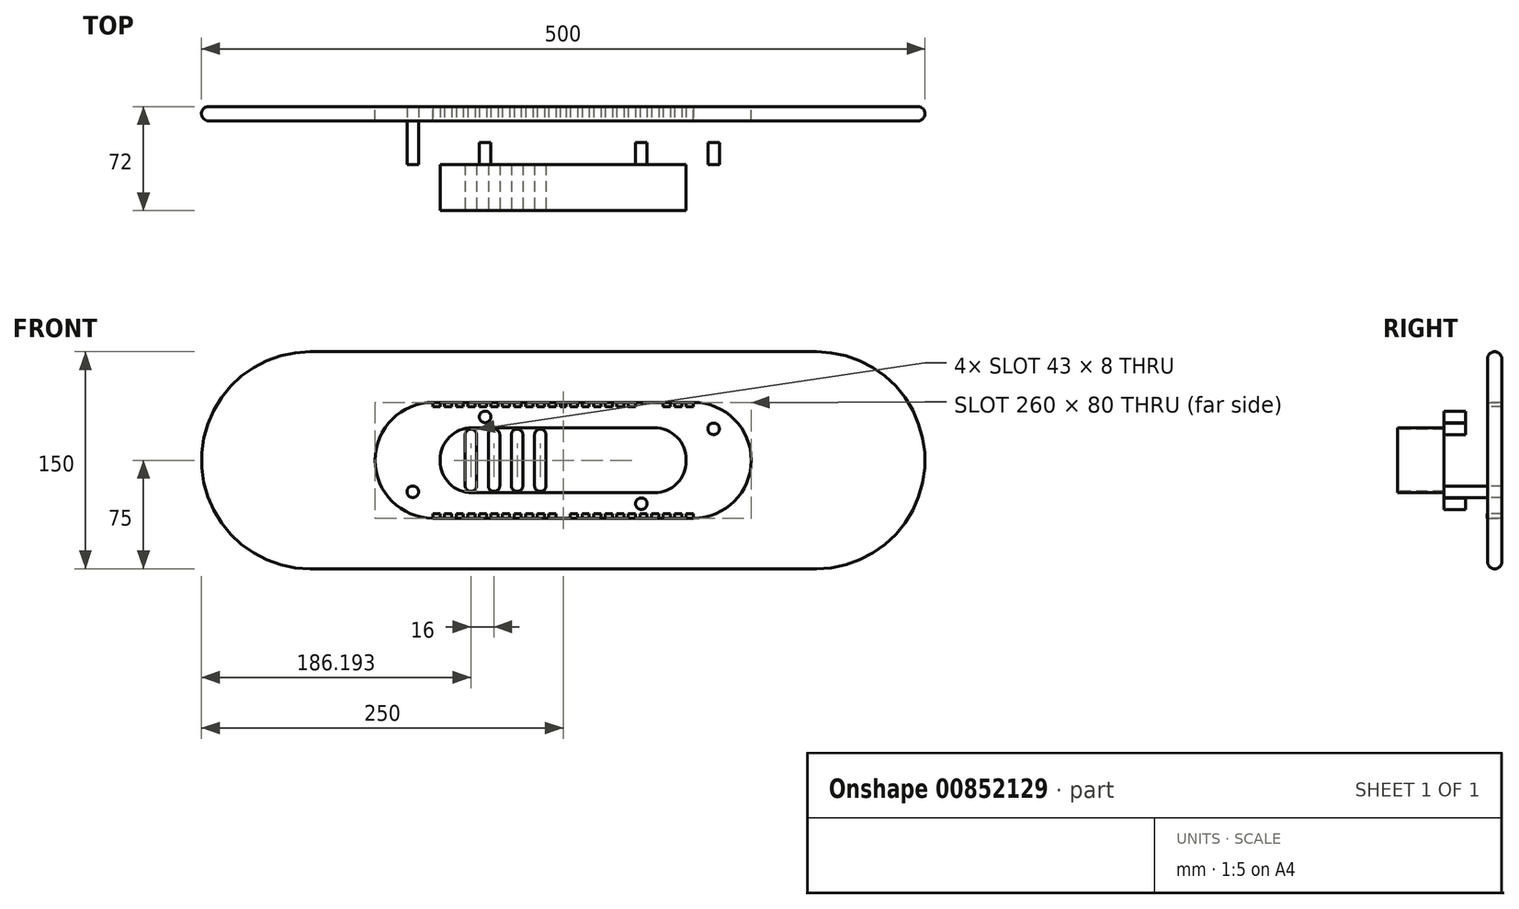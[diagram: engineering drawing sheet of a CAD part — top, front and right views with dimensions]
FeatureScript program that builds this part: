
annotation { "Feature Type Name" : "Feature", "Feature Type Description" : "" }
export const myFeature = defineFeature(function(context is Context, id is Id, definition is map)
    precondition{}
    {
        {
            var Q0;
            Q0=qCreatedBy(makeId("Front.planeOp"),FACE);
            var sketch = newSketch(context, id + "F0", { "sketchPlane" : qUnion([Q0])});
            skLineSegment(sketch, "E0.bottom", {"start": v(175, -75) * mm, "end": v(-175, -75) * mm});
            skLineSegment(sketch, "E0.top", {"start": v(175, 75) * mm, "end": v(-175, 75) * mm});
            skLineSegment(sketch, "E0.left", {"start": v(250, 0) * mm, "end": v(250, 0) * mm});
            skLineSegment(sketch, "E0.right", {"start": v(-250, 0) * mm, "end": v(-250, 0) * mm});
            skPoint(sketch, "E0.middle", {"position": v(0, 0) * mm});
            skPoint(sketch, "E1.visualSharp", {"position": v(-250, 75) * mm});
            skArc(sketch, "E1.filletArc", {"start": v(-175, 75) * mm, "mid": v(-228.03, 53.03) * mm, "end": v(-250, 0) * mm});
            skPoint(sketch, "E2.visualSharp", {"position": v(-250, -75) * mm});
            skArc(sketch, "E2.filletArc", {"start": v(-250, 0) * mm, "mid": v(-228.03, -53.03) * mm, "end": v(-175, -75) * mm});
            skPoint(sketch, "E3.visualSharp", {"position": v(250, -75) * mm});
            skArc(sketch, "E3.filletArc", {"start": v(175, -75) * mm, "mid": v(228.03, -53.03) * mm, "end": v(250, 0) * mm});
            skPoint(sketch, "E4.visualSharp", {"position": v(250, 75) * mm});
            skArc(sketch, "E4.filletArc", {"start": v(250, 0) * mm, "mid": v(228.03, 53.03) * mm, "end": v(175, 75) * mm});
            skLineSegment(sketch, "E5.bottom", {"start": v(90, -40) * mm, "end": v(-90, -40) * mm});
            skLineSegment(sketch, "E5.top", {"start": v(90, 40) * mm, "end": v(-90, 40) * mm});
            skLineSegment(sketch, "E5.left", {"start": v(130, 0) * mm, "end": v(130, 0) * mm});
            skLineSegment(sketch, "E5.right", {"start": v(-130, 0) * mm, "end": v(-130, 0) * mm});
            skPoint(sketch, "E6.visualSharp", {"position": v(-130, 40) * mm});
            skArc(sketch, "E6.filletArc", {"start": v(-90, 40) * mm, "mid": v(-118.28, 28.28) * mm, "end": v(-130, 0) * mm});
            skPoint(sketch, "E7.visualSharp", {"position": v(-130, -40) * mm});
            skArc(sketch, "E7.filletArc", {"start": v(-130, 0) * mm, "mid": v(-118.28, -28.28) * mm, "end": v(-90, -40) * mm});
            skPoint(sketch, "E8.visualSharp", {"position": v(130, 40) * mm});
            skArc(sketch, "E8.filletArc", {"start": v(130, 0) * mm, "mid": v(118.28, 28.28) * mm, "end": v(90, 40) * mm});
            skPoint(sketch, "E9.visualSharp", {"position": v(130, -40) * mm});
            skArc(sketch, "E9.filletArc", {"start": v(90, -40) * mm, "mid": v(118.28, -28.28) * mm, "end": v(130, 0) * mm});
            skLineSegment(sketch, "E10.bottom", {"start": v(63, -22.5) * mm, "end": v(-63, -22.5) * mm});
            skLineSegment(sketch, "E10.top", {"start": v(63, 22.5) * mm, "end": v(-63, 22.5) * mm});
            skLineSegment(sketch, "E10.left", {"start": v(85, -0.5) * mm, "end": v(85, 0.5) * mm});
            skLineSegment(sketch, "E10.right", {"start": v(-85, -0.5) * mm, "end": v(-85, 0.5) * mm});
            skPoint(sketch, "E11.visualSharp", {"position": v(-85, 22.5) * mm});
            skArc(sketch, "E11.filletArc", {"start": v(-63, 22.5) * mm, "mid": v(-78.56, 16.06) * mm, "end": v(-85, 0.5) * mm});
            skPoint(sketch, "E12.visualSharp", {"position": v(-85, -22.5) * mm});
            skArc(sketch, "E12.filletArc", {"start": v(-85, -0.5) * mm, "mid": v(-78.56, -16.06) * mm, "end": v(-63, -22.5) * mm});
            skPoint(sketch, "E13.visualSharp", {"position": v(85, -22.5) * mm});
            skArc(sketch, "E13.filletArc", {"start": v(63, -22.5) * mm, "mid": v(78.56, -16.06) * mm, "end": v(85, -0.5) * mm});
            skPoint(sketch, "E14.visualSharp", {"position": v(85, 22.5) * mm});
            skArc(sketch, "E14.filletArc", {"start": v(85, 0.5) * mm, "mid": v(78.56, 16.06) * mm, "end": v(63, 22.5) * mm});
            skSolve(sketch);
        }
        {
            var Q0;
            Q0=makeQuery(id+"F0.imprint","IMPRINT",FACE,{"disambiguationData":[TD([[makeQuery(id+"F0.imprint","IMPRINT",EDGE,{"derivedFrom":sQuery(id+"F0.wireOp",EDGE,"E0.bottom")}),-1.0]])]});
            extrude(context, id + "F1", {"entities" : qUnion([Q0]), "depth" : 10 * mm, "offsetDistance" : 25 * mm});
        }
        {
            var Q0;
            Q0=makeQuery(id+"F0.imprint","IMPRINT",FACE,{"disambiguationData":[TD([[makeQuery(id+"F0.imprint","IMPRINT",EDGE,{"derivedFrom":sQuery(id+"F0.wireOp",EDGE,"E5.bottom")}),-1.0]])]});
            extrude(context, id + "F2", {"entities" : qUnion([Q0]), "depth" : 40 * mm, "offsetDistance" : 25 * mm});
        }
        {
            var Q0;
            Q0=makeQuery(id+"F0.imprint","IMPRINT",FACE,{"disambiguationData":[TD([[makeQuery(id+"F0.imprint","IMPRINT",EDGE,{"derivedFrom":sQuery(id+"F0.wireOp",EDGE,"E10.bottom")}),-1.0]])]});
            extrude(context, id + "F3", {"entities" : qUnion([Q0]), "depth" : 72 * mm, "offsetDistance" : 25 * mm});
        }
        {
            var Q0;
            Q0=makeQuery(id+"F1.opExtrude","CAP_EDGE",EDGE,{"disambiguationData":[OSD([sQuery(id+"F0.wireOp",EDGE,"E1.filletArc"),sQuery(id+"F0.wireOp",EDGE,"E2.filletArc")])],"isStart":true});
            var Q1;
            Q1=makeQuery(id+"F1.opExtrude","CAP_EDGE",EDGE,{"disambiguationData":[OSD([sQuery(id+"F0.wireOp",EDGE,"E1.filletArc"),sQuery(id+"F0.wireOp",EDGE,"E2.filletArc")])],"isStart":false});
            fillet(context, id + "F4", {"entities" : qUnion([Q0, Q1]), "radius" : 5 * mm, "tangentPropagation" : true, "allowEdgeOverflow" : false});
        }
        {
            var Q0;
            Q0=makeQuery(id+"F2.opExtrude","SWEPT_FACE",FACE,{"disambiguationData":[OSD([sQuery(id+"F0.wireOp",EDGE,"E5.bottom")])]});
            var sketch = newSketch(context, id + "F5", { "sketchPlane" : qUnion([Q0])});
            skLineSegment(sketch, "E15.bottom", {"start": v(-90, 40) * mm, "end": v(-1.81, 40) * mm});
            skLineSegment(sketch, "E15.top", {"start": v(-90, 10.14) * mm, "end": v(-1.81, 10.14) * mm});
            skLineSegment(sketch, "E15.left", {"start": v(-90, 40) * mm, "end": v(-90, 10.14) * mm});
            skLineSegment(sketch, "E15.right", {"start": v(90, 40) * mm, "end": v(90, 10.14) * mm});
            skLineSegment(sketch, "E16.bottom", {"start": v(-85, 40) * mm, "end": v(-82, 40) * mm});
            skLineSegment(sketch, "E16.top", {"start": v(-85, 10.14) * mm, "end": v(-82, 10.14) * mm});
            skLineSegment(sketch, "E16.left", {"start": v(-85, 40) * mm, "end": v(-85, 10.14) * mm});
            skLineSegment(sketch, "E16.right", {"start": v(-82, 40) * mm, "end": v(-82, 10.14) * mm});
            skLineSegment(sketch, "E17.bottom", {"start": v(-77, 40) * mm, "end": v(-74, 40) * mm});
            skLineSegment(sketch, "E17.top", {"start": v(-77, 10.14) * mm, "end": v(-74, 10.14) * mm});
            skLineSegment(sketch, "E17.left", {"start": v(-77, 40) * mm, "end": v(-77, 10.14) * mm});
            skLineSegment(sketch, "E17.right", {"start": v(-74, 40) * mm, "end": v(-74, 10.14) * mm});
            skLineSegment(sketch, "E18.bottom", {"start": v(-69, 40) * mm, "end": v(-66, 40) * mm});
            skLineSegment(sketch, "E18.top", {"start": v(-69, 10.14) * mm, "end": v(-66, 10.14) * mm});
            skLineSegment(sketch, "E18.left", {"start": v(-69, 40) * mm, "end": v(-69, 10.14) * mm});
            skLineSegment(sketch, "E18.right", {"start": v(-66, 40) * mm, "end": v(-66, 10.14) * mm});
            skLineSegment(sketch, "E19.bottom", {"start": v(-61, 40) * mm, "end": v(-58, 40) * mm});
            skLineSegment(sketch, "E19.top", {"start": v(-61, 10.14) * mm, "end": v(-58, 10.14) * mm});
            skLineSegment(sketch, "E19.left", {"start": v(-61, 40) * mm, "end": v(-61, 10.14) * mm});
            skLineSegment(sketch, "E19.right", {"start": v(-58, 40) * mm, "end": v(-58, 10.14) * mm});
            skLineSegment(sketch, "E20.bottom", {"start": v(-53, 40) * mm, "end": v(-50, 40) * mm});
            skLineSegment(sketch, "E20.top", {"start": v(-53, 10.14) * mm, "end": v(-50, 10.14) * mm});
            skLineSegment(sketch, "E20.left", {"start": v(-53, 40) * mm, "end": v(-53, 10.14) * mm});
            skLineSegment(sketch, "E20.right", {"start": v(-50, 40) * mm, "end": v(-50, 10.14) * mm});
            skLineSegment(sketch, "E21.bottom", {"start": v(-45, 40) * mm, "end": v(-42, 40) * mm});
            skLineSegment(sketch, "E21.top", {"start": v(-45, 10.14) * mm, "end": v(-42, 10.14) * mm});
            skLineSegment(sketch, "E21.left", {"start": v(-42, 40) * mm, "end": v(-42, 10.14) * mm});
            skLineSegment(sketch, "E21.right", {"start": v(-45, 40) * mm, "end": v(-45, 10.14) * mm});
            skLineSegment(sketch, "E22.bottom", {"start": v(-37, 40) * mm, "end": v(-34, 40) * mm});
            skLineSegment(sketch, "E22.top", {"start": v(-37, 10.14) * mm, "end": v(-34, 10.14) * mm});
            skLineSegment(sketch, "E22.left", {"start": v(-37, 40) * mm, "end": v(-37, 10.14) * mm});
            skLineSegment(sketch, "E22.right", {"start": v(-34, 40) * mm, "end": v(-34, 10.14) * mm});
            skLineSegment(sketch, "E23.bottom", {"start": v(-29, 40) * mm, "end": v(-26, 40) * mm});
            skLineSegment(sketch, "E23.top", {"start": v(-29, 10.14) * mm, "end": v(-26, 10.14) * mm});
            skLineSegment(sketch, "E23.left", {"start": v(-29, 40) * mm, "end": v(-29, 10.14) * mm});
            skLineSegment(sketch, "E23.right", {"start": v(-26, 40) * mm, "end": v(-26, 10.14) * mm});
            skLineSegment(sketch, "E24.bottom", {"start": v(-21, 40) * mm, "end": v(-18, 40) * mm});
            skLineSegment(sketch, "E24.top", {"start": v(-21, 10.14) * mm, "end": v(-18, 10.14) * mm});
            skLineSegment(sketch, "E24.left", {"start": v(-21, 40) * mm, "end": v(-21, 10.14) * mm});
            skLineSegment(sketch, "E24.right", {"start": v(-18, 40) * mm, "end": v(-18, 10.14) * mm});
            skLineSegment(sketch, "E25.bottom", {"start": v(-13, 40) * mm, "end": v(-10, 40) * mm});
            skLineSegment(sketch, "E25.top", {"start": v(-13, 10.14) * mm, "end": v(-10, 10.14) * mm});
            skLineSegment(sketch, "E25.left", {"start": v(-13, 40) * mm, "end": v(-13, 10.14) * mm});
            skLineSegment(sketch, "E25.right", {"start": v(-10, 40) * mm, "end": v(-10, 10.14) * mm});
            skLineSegment(sketch, "E26.bottom", {"start": v(-5, 40) * mm, "end": v(1.84, 40) * mm});
            skLineSegment(sketch, "E26.top", {"start": v(-5, 10.14) * mm, "end": v(1.84, 10.14) * mm});
            skLineSegment(sketch, "E26.left", {"start": v(-5, 40) * mm, "end": v(-5, 10.14) * mm});
            skLineSegment(sketch, "E27.bottom", {"start": v(-2, 40) * mm, "end": v(-1.81, 40) * mm});
            skLineSegment(sketch, "E27.top", {"start": v(-2, 10.14) * mm, "end": v(-1.81, 10.14) * mm});
            skLineSegment(sketch, "E27.left", {"start": v(-2, 40) * mm, "end": v(-2, 10.14) * mm});
            skLineSegment(sketch, "E28.trimOffspring", {"start": v(1.84, 10.14) * mm, "end": v(90, 10.14) * mm});
            skLineSegment(sketch, "E29.trimOffspring", {"start": v(1.84, 40) * mm, "end": v(90, 40) * mm});
            skLineSegment(sketch, "E30.MirrorCS", {"start": v(2, 10.14) * mm, "end": v(1.81, 10.14) * mm});
            skLineSegment(sketch, "E31.MirrorCS", {"start": v(2, 40) * mm, "end": v(1.81, 40) * mm});
            skLineSegment(sketch, "E32.MirrorCS", {"start": v(45, 40) * mm, "end": v(42, 40) * mm});
            skLineSegment(sketch, "E33.MirrorCS", {"start": v(53, 10.14) * mm, "end": v(50, 10.14) * mm});
            skLineSegment(sketch, "E34.MirrorCS", {"start": v(21, 40) * mm, "end": v(18, 40) * mm});
            skLineSegment(sketch, "E35.MirrorCS", {"start": v(90, 10.14) * mm, "end": v(1.81, 10.14) * mm});
            skLineSegment(sketch, "E36.MirrorCS", {"start": v(53, 40) * mm, "end": v(50, 40) * mm});
            skLineSegment(sketch, "E37.MirrorCS", {"start": v(13, 10.14) * mm, "end": v(10, 10.14) * mm});
            skLineSegment(sketch, "E38.MirrorCS", {"start": v(61, 10.14) * mm, "end": v(58, 10.14) * mm});
            skLineSegment(sketch, "E39.MirrorCS", {"start": v(77, 40) * mm, "end": v(74, 40) * mm});
            skLineSegment(sketch, "E40.MirrorCS", {"start": v(37, 40) * mm, "end": v(34, 40) * mm});
            skLineSegment(sketch, "E41.MirrorCS", {"start": v(69, 10.14) * mm, "end": v(66, 10.14) * mm});
            skLineSegment(sketch, "E42.MirrorCS", {"start": v(21, 10.14) * mm, "end": v(18, 10.14) * mm});
            skLineSegment(sketch, "E43.MirrorCS", {"start": v(29, 40) * mm, "end": v(26, 40) * mm});
            skLineSegment(sketch, "E44.MirrorCS", {"start": v(85, 10.14) * mm, "end": v(82, 10.14) * mm});
            skLineSegment(sketch, "E45.MirrorCS", {"start": v(29, 10.14) * mm, "end": v(26, 10.14) * mm});
            skLineSegment(sketch, "E46.MirrorCS", {"start": v(69, 40) * mm, "end": v(66, 40) * mm});
            skLineSegment(sketch, "E47.MirrorCS", {"start": v(90, 40) * mm, "end": v(1.81, 40) * mm});
            skLineSegment(sketch, "E48.MirrorCS", {"start": v(85, 40) * mm, "end": v(82, 40) * mm});
            skLineSegment(sketch, "E49.MirrorCS", {"start": v(13, 40) * mm, "end": v(10, 40) * mm});
            skLineSegment(sketch, "E50.MirrorCS", {"start": v(45, 10.14) * mm, "end": v(42, 10.14) * mm});
            skLineSegment(sketch, "E51.MirrorCS", {"start": v(61, 40) * mm, "end": v(58, 40) * mm});
            skLineSegment(sketch, "E52.MirrorCS", {"start": v(77, 10.14) * mm, "end": v(74, 10.14) * mm});
            skLineSegment(sketch, "E53.MirrorCS", {"start": v(37, 10.14) * mm, "end": v(34, 10.14) * mm});
            skLineSegment(sketch, "E54.MirrorCS", {"start": v(66, 40) * mm, "end": v(66, 10.14) * mm});
            skLineSegment(sketch, "E55.MirrorCS", {"start": v(61, 40) * mm, "end": v(61, 10.14) * mm});
            skLineSegment(sketch, "E56.MirrorCS", {"start": v(58, 40) * mm, "end": v(58, 10.14) * mm});
            skLineSegment(sketch, "E57.MirrorCS", {"start": v(50, 40) * mm, "end": v(50, 10.14) * mm});
            skLineSegment(sketch, "E58.MirrorCS", {"start": v(13, 40) * mm, "end": v(13, 10.14) * mm});
            skLineSegment(sketch, "E59.MirrorCS", {"start": v(2, 40) * mm, "end": v(2, 10.14) * mm});
            skLineSegment(sketch, "E60.MirrorCS", {"start": v(21, 40) * mm, "end": v(21, 10.14) * mm});
            skLineSegment(sketch, "E61.MirrorCS", {"start": v(45, 40) * mm, "end": v(45, 10.14) * mm});
            skLineSegment(sketch, "E62.MirrorCS", {"start": v(37, 40) * mm, "end": v(37, 10.14) * mm});
            skLineSegment(sketch, "E63.MirrorCS", {"start": v(85, 40) * mm, "end": v(85, 10.14) * mm});
            skLineSegment(sketch, "E64.MirrorCS", {"start": v(42, 40) * mm, "end": v(42, 10.14) * mm});
            skLineSegment(sketch, "E65.MirrorCS", {"start": v(18, 40) * mm, "end": v(18, 10.14) * mm});
            skLineSegment(sketch, "E66.MirrorCS", {"start": v(26, 40) * mm, "end": v(26, 10.14) * mm});
            skLineSegment(sketch, "E67.MirrorCS", {"start": v(29, 40) * mm, "end": v(29, 10.14) * mm});
            skLineSegment(sketch, "E68.MirrorCS", {"start": v(77, 40) * mm, "end": v(77, 10.14) * mm});
            skLineSegment(sketch, "E69.MirrorCS", {"start": v(10, 40) * mm, "end": v(10, 10.14) * mm});
            skLineSegment(sketch, "E70.MirrorCS", {"start": v(34, 40) * mm, "end": v(34, 10.14) * mm});
            skLineSegment(sketch, "E71.MirrorCS", {"start": v(82, 40) * mm, "end": v(82, 10.14) * mm});
            skLineSegment(sketch, "E72.MirrorCS", {"start": v(53, 40) * mm, "end": v(53, 10.14) * mm});
            skLineSegment(sketch, "E73.MirrorCS", {"start": v(74, 40) * mm, "end": v(74, 10.14) * mm});
            skLineSegment(sketch, "E74.MirrorCS", {"start": v(5, 40) * mm, "end": v(5, 10.14) * mm});
            skLineSegment(sketch, "E75.MirrorCS", {"start": v(69, 40) * mm, "end": v(69, 10.14) * mm});
            skSolve(sketch);
        }
        {
            var Q0;
            {var subQ0=sQuery(id+"F5.wireOp",EDGE,"E15.left");Q0=makeQuery(id+"F5.imprint","IMPRINT",FACE,{"disambiguationData":[TD([[makeQuery(id+"F5.imprint","IMPRINT",EDGE,{"derivedFrom":subQ0}),1.0]])]});}
            var Q1;
            {var subQ0=sQuery(id+"F5.wireOp",EDGE,"E16.right");Q1=makeQuery(id+"F5.imprint","IMPRINT",FACE,{"disambiguationData":[TD([[makeQuery(id+"F5.imprint","IMPRINT",EDGE,{"derivedFrom":subQ0}),1.0]])]});}
            var Q2;
            {var subQ0=sQuery(id+"F5.wireOp",EDGE,"E17.right");Q2=makeQuery(id+"F5.imprint","IMPRINT",FACE,{"disambiguationData":[TD([[makeQuery(id+"F5.imprint","IMPRINT",EDGE,{"derivedFrom":subQ0}),1.0]])]});}
            var Q3;
            {var subQ0=sQuery(id+"F5.wireOp",EDGE,"E18.right");Q3=makeQuery(id+"F5.imprint","IMPRINT",FACE,{"disambiguationData":[TD([[makeQuery(id+"F5.imprint","IMPRINT",EDGE,{"derivedFrom":subQ0}),1.0]])]});}
            var Q4;
            {var subQ0=sQuery(id+"F5.wireOp",EDGE,"E19.right");Q4=makeQuery(id+"F5.imprint","IMPRINT",FACE,{"disambiguationData":[TD([[makeQuery(id+"F5.imprint","IMPRINT",EDGE,{"derivedFrom":subQ0}),1.0]])]});}
            var Q5;
            {var subQ0=sQuery(id+"F5.wireOp",EDGE,"E20.right");Q5=makeQuery(id+"F5.imprint","IMPRINT",FACE,{"disambiguationData":[TD([[makeQuery(id+"F5.imprint","IMPRINT",EDGE,{"derivedFrom":subQ0}),1.0]])]});}
            var Q6;
            {var subQ0=sQuery(id+"F5.wireOp",EDGE,"E21.left");Q6=makeQuery(id+"F5.imprint","IMPRINT",FACE,{"disambiguationData":[TD([[makeQuery(id+"F5.imprint","IMPRINT",EDGE,{"derivedFrom":subQ0}),1.0]])]});}
            var Q7;
            {var subQ0=sQuery(id+"F5.wireOp",EDGE,"E22.right");Q7=makeQuery(id+"F5.imprint","IMPRINT",FACE,{"disambiguationData":[TD([[makeQuery(id+"F5.imprint","IMPRINT",EDGE,{"derivedFrom":subQ0}),1.0]])]});}
            var Q8;
            {var subQ0=sQuery(id+"F5.wireOp",EDGE,"E23.right");Q8=makeQuery(id+"F5.imprint","IMPRINT",FACE,{"disambiguationData":[TD([[makeQuery(id+"F5.imprint","IMPRINT",EDGE,{"derivedFrom":subQ0}),1.0]])]});}
            var Q9;
            {var subQ0=sQuery(id+"F5.wireOp",EDGE,"E24.right");Q9=makeQuery(id+"F5.imprint","IMPRINT",FACE,{"disambiguationData":[TD([[makeQuery(id+"F5.imprint","IMPRINT",EDGE,{"derivedFrom":subQ0}),1.0]])]});}
            var Q10;
            {var subQ2=sQuery(id+"F5.wireOp",EDGE,"E25.right");Q10=makeQuery(id+"F5.imprint","IMPRINT",FACE,{"disambiguationData":[TD([[makeQuery(id+"F5.imprint","IMPRINT",EDGE,{"derivedFrom":subQ2}),1.0]])]});}
            var Q11;
            {var subQ8=sQuery(id+"F5.wireOp",EDGE,"E27.bottom");Q11=makeQuery(id+"F5.imprint","IMPRINT",FACE,{"disambiguationData":[TD([[makeQuery(id+"F5.imprint","IMPRINT",EDGE,{"derivedFrom":subQ8}),1.0]])]});}
            var Q12;
            {var subQ0=sQuery(id+"F5.wireOp",EDGE,"E69.MirrorCS");Q12=makeQuery(id+"F5.imprint","IMPRINT",FACE,{"disambiguationData":[TD([[makeQuery(id+"F5.imprint","IMPRINT",EDGE,{"derivedFrom":subQ0}),-1.0]])]});}
            var Q13;
            {var subQ0=sQuery(id+"F5.wireOp",EDGE,"E58.MirrorCS");Q13=makeQuery(id+"F5.imprint","IMPRINT",FACE,{"disambiguationData":[TD([[makeQuery(id+"F5.imprint","IMPRINT",EDGE,{"derivedFrom":subQ0}),1.0]])]});}
            var Q14;
            {var subQ0=sQuery(id+"F5.wireOp",EDGE,"E60.MirrorCS");Q14=makeQuery(id+"F5.imprint","IMPRINT",FACE,{"disambiguationData":[TD([[makeQuery(id+"F5.imprint","IMPRINT",EDGE,{"derivedFrom":subQ0}),1.0]])]});}
            var Q15;
            {var subQ0=sQuery(id+"F5.wireOp",EDGE,"E67.MirrorCS");Q15=makeQuery(id+"F5.imprint","IMPRINT",FACE,{"disambiguationData":[TD([[makeQuery(id+"F5.imprint","IMPRINT",EDGE,{"derivedFrom":subQ0}),1.0]])]});}
            var Q16;
            {var subQ2=sQuery(id+"F5.wireOp",EDGE,"E62.MirrorCS");Q16=makeQuery(id+"F5.imprint","IMPRINT",FACE,{"disambiguationData":[TD([[makeQuery(id+"F5.imprint","IMPRINT",EDGE,{"derivedFrom":subQ2}),1.0]])]});}
            var Q17;
            {var subQ2=sQuery(id+"F5.wireOp",EDGE,"E57.MirrorCS");Q17=makeQuery(id+"F5.imprint","IMPRINT",FACE,{"disambiguationData":[TD([[makeQuery(id+"F5.imprint","IMPRINT",EDGE,{"derivedFrom":subQ2}),-1.0]])]});}
            var Q18;
            {var subQ0=sQuery(id+"F5.wireOp",EDGE,"E56.MirrorCS");Q18=makeQuery(id+"F5.imprint","IMPRINT",FACE,{"disambiguationData":[TD([[makeQuery(id+"F5.imprint","IMPRINT",EDGE,{"derivedFrom":subQ0}),-1.0]])]});}
            var Q19;
            {var subQ2=sQuery(id+"F5.wireOp",EDGE,"E54.MirrorCS");Q19=makeQuery(id+"F5.imprint","IMPRINT",FACE,{"disambiguationData":[TD([[makeQuery(id+"F5.imprint","IMPRINT",EDGE,{"derivedFrom":subQ2}),-1.0]])]});}
            var Q20;
            {var subQ2=sQuery(id+"F5.wireOp",EDGE,"E73.MirrorCS");Q20=makeQuery(id+"F5.imprint","IMPRINT",FACE,{"disambiguationData":[TD([[makeQuery(id+"F5.imprint","IMPRINT",EDGE,{"derivedFrom":subQ2}),-1.0]])]});}
            var Q21;
            {var subQ2=sQuery(id+"F5.wireOp",EDGE,"E68.MirrorCS");Q21=makeQuery(id+"F5.imprint","IMPRINT",FACE,{"disambiguationData":[TD([[makeQuery(id+"F5.imprint","IMPRINT",EDGE,{"derivedFrom":subQ2}),1.0]])]});}
            var Q22;
            {var subQ2=sQuery(id+"F5.wireOp",EDGE,"E63.MirrorCS");Q22=makeQuery(id+"F5.imprint","IMPRINT",FACE,{"disambiguationData":[TD([[makeQuery(id+"F5.imprint","IMPRINT",EDGE,{"derivedFrom":subQ2}),1.0]])]});}
            extrude(context, id + "F6", {"entities" : qUnion([Q0, Q1, Q2, Q3, Q4, Q5, Q6, Q7, Q8, Q9, Q10, Q11, Q12, Q13, Q14, Q15, Q16, Q17, Q18, Q19, Q20, Q21, Q22]), "operationType" : NewBodyOperationType.REMOVE, "oppositeDirection" : true, "depth" : 3 * mm, "offsetDistance" : 25 * mm});
        }
        {
            var Q0;
            Q0=makeQuery(id+"F2.opExtrude","SWEPT_FACE",FACE,{"disambiguationData":[OSD([sQuery(id+"F0.wireOp",EDGE,"E5.top")])]});
            var sketch = newSketch(context, id + "F7", { "sketchPlane" : qUnion([Q0])});
            skLineSegment(sketch, "E76.bottom", {"start": v(90, -40) * mm, "end": v(5, -40) * mm});
            skLineSegment(sketch, "E76.top", {"start": v(90, -9.96) * mm, "end": v(5, -9.96) * mm});
            skLineSegment(sketch, "E76.left", {"start": v(90, -40) * mm, "end": v(90, -9.96) * mm});
            skLineSegment(sketch, "E76.right", {"start": v(-90, -40) * mm, "end": v(-90, -9.96) * mm});
            skLineSegment(sketch, "E77.bottom", {"start": v(85, -40) * mm, "end": v(82, -40) * mm});
            skLineSegment(sketch, "E77.top", {"start": v(85, -9.96) * mm, "end": v(82, -9.96) * mm});
            skLineSegment(sketch, "E77.left", {"start": v(85, -40) * mm, "end": v(85, -9.96) * mm});
            skLineSegment(sketch, "E77.right", {"start": v(82, -40) * mm, "end": v(82, -9.96) * mm});
            skLineSegment(sketch, "E78.bottom", {"start": v(77, -40) * mm, "end": v(74, -40) * mm});
            skLineSegment(sketch, "E78.top", {"start": v(77, -9.96) * mm, "end": v(74, -9.96) * mm});
            skLineSegment(sketch, "E78.left", {"start": v(77, -40) * mm, "end": v(77, -9.96) * mm});
            skLineSegment(sketch, "E78.right", {"start": v(74, -40) * mm, "end": v(74, -9.96) * mm});
            skLineSegment(sketch, "E79.bottom", {"start": v(69, -40) * mm, "end": v(50, -40) * mm});
            skLineSegment(sketch, "E79.top", {"start": v(69, -9.96) * mm, "end": v(50, -9.96) * mm});
            skLineSegment(sketch, "E79.left", {"start": v(69, -40) * mm, "end": v(69, -9.96) * mm});
            skLineSegment(sketch, "E79.right", {"start": v(50, -40) * mm, "end": v(50, -9.96) * mm});
            skLineSegment(sketch, "E80.bottom", {"start": v(37, -40) * mm, "end": v(34, -40) * mm});
            skLineSegment(sketch, "E80.top", {"start": v(37, -9.96) * mm, "end": v(34, -9.96) * mm});
            skLineSegment(sketch, "E80.left", {"start": v(37, -40) * mm, "end": v(37, -9.96) * mm});
            skLineSegment(sketch, "E80.right", {"start": v(34, -40) * mm, "end": v(34, -9.96) * mm});
            skLineSegment(sketch, "E81.bottom", {"start": v(66, -40) * mm, "end": v(61, -40) * mm});
            skLineSegment(sketch, "E81.top", {"start": v(66, -9.96) * mm, "end": v(61, -9.96) * mm});
            skLineSegment(sketch, "E81.left", {"start": v(66, -40) * mm, "end": v(66, -9.96) * mm});
            skLineSegment(sketch, "E81.right", {"start": v(61, -40) * mm, "end": v(61, -9.96) * mm});
            skLineSegment(sketch, "E82.bottom", {"start": v(58, -40) * mm, "end": v(53, -40) * mm});
            skLineSegment(sketch, "E82.top", {"start": v(58, -9.96) * mm, "end": v(53, -9.96) * mm});
            skLineSegment(sketch, "E82.left", {"start": v(58, -40) * mm, "end": v(58, -9.96) * mm});
            skLineSegment(sketch, "E82.right", {"start": v(53, -40) * mm, "end": v(53, -9.96) * mm});
            skLineSegment(sketch, "E83.bottom", {"start": v(45, -40) * mm, "end": v(42, -40) * mm});
            skLineSegment(sketch, "E83.top", {"start": v(45, -9.96) * mm, "end": v(42, -9.96) * mm});
            skLineSegment(sketch, "E83.left", {"start": v(45, -40) * mm, "end": v(45, -9.96) * mm});
            skLineSegment(sketch, "E83.right", {"start": v(42, -40) * mm, "end": v(42, -9.96) * mm});
            skLineSegment(sketch, "E84.bottom", {"start": v(29, -40) * mm, "end": v(26, -40) * mm});
            skLineSegment(sketch, "E84.top", {"start": v(29, -9.96) * mm, "end": v(26, -9.96) * mm});
            skLineSegment(sketch, "E84.left", {"start": v(29, -40) * mm, "end": v(29, -9.96) * mm});
            skLineSegment(sketch, "E84.right", {"start": v(26, -40) * mm, "end": v(26, -9.96) * mm});
            skLineSegment(sketch, "E85.bottom", {"start": v(21, -40) * mm, "end": v(18, -40) * mm});
            skLineSegment(sketch, "E85.top", {"start": v(21, -9.96) * mm, "end": v(18, -9.96) * mm});
            skLineSegment(sketch, "E85.left", {"start": v(21, -40) * mm, "end": v(21, -9.96) * mm});
            skLineSegment(sketch, "E85.right", {"start": v(18, -40) * mm, "end": v(18, -9.96) * mm});
            skLineSegment(sketch, "E86.bottom", {"start": v(13, -40) * mm, "end": v(10, -40) * mm});
            skLineSegment(sketch, "E86.top", {"start": v(13, -9.96) * mm, "end": v(10, -9.96) * mm});
            skLineSegment(sketch, "E86.left", {"start": v(13, -40) * mm, "end": v(13, -9.96) * mm});
            skLineSegment(sketch, "E86.right", {"start": v(10, -40) * mm, "end": v(10, -9.96) * mm});
            skLineSegment(sketch, "E87.bottom", {"start": v(5, -40) * mm, "end": v(-1, -40) * mm});
            skLineSegment(sketch, "E87.left", {"start": v(5, -40) * mm, "end": v(5, -9.96) * mm});
            skLineSegment(sketch, "E88.trimOffspring", {"start": v(-1, -40) * mm, "end": v(-90, -40) * mm});
            skLineSegment(sketch, "E89.trimOffspring", {"start": v(0, -9.96) * mm, "end": v(-90, -9.96) * mm});
            skLineSegment(sketch, "E90", {"start": v(2, -40) * mm, "end": v(2, -9.86) * mm});
            skLineSegment(sketch, "E91", {"start": v(2, -9.86) * mm, "end": v(5, -9.96) * mm});
            skLineSegment(sketch, "E92.MirrorCS", {"start": v(-2, -9.86) * mm, "end": v(-5, -9.96) * mm});
            skLineSegment(sketch, "E93.MirrorCS", {"start": v(-29, -9.96) * mm, "end": v(-26, -9.96) * mm});
            skLineSegment(sketch, "E94.MirrorCS", {"start": v(-37, -40) * mm, "end": v(-34, -40) * mm});
            skLineSegment(sketch, "E95.MirrorCS", {"start": v(-29, -40) * mm, "end": v(-26, -40) * mm});
            skLineSegment(sketch, "E96.MirrorCS", {"start": v(-45, -40) * mm, "end": v(-42, -40) * mm});
            skLineSegment(sketch, "E97.MirrorCS", {"start": v(-69, -40) * mm, "end": v(-50, -40) * mm});
            skLineSegment(sketch, "E98.MirrorCS", {"start": v(-77, -9.96) * mm, "end": v(-74, -9.96) * mm});
            skLineSegment(sketch, "E99.MirrorCS", {"start": v(-13, -9.96) * mm, "end": v(-10, -9.96) * mm});
            skLineSegment(sketch, "E100.MirrorCS", {"start": v(-58, -9.96) * mm, "end": v(-53, -9.96) * mm});
            skLineSegment(sketch, "E101.MirrorCS", {"start": v(-13, -40) * mm, "end": v(-10, -40) * mm});
            skLineSegment(sketch, "E102.MirrorCS", {"start": v(-58, -40) * mm, "end": v(-53, -40) * mm});
            skLineSegment(sketch, "E103.MirrorCS", {"start": v(-69, -9.96) * mm, "end": v(-50, -9.96) * mm});
            skLineSegment(sketch, "E104.MirrorCS", {"start": v(-66, -9.96) * mm, "end": v(-61, -9.96) * mm});
            skLineSegment(sketch, "E105.MirrorCS", {"start": v(-66, -40) * mm, "end": v(-61, -40) * mm});
            skLineSegment(sketch, "E106.MirrorCS", {"start": v(-21, -9.96) * mm, "end": v(-18, -9.96) * mm});
            skLineSegment(sketch, "E107.MirrorCS", {"start": v(-77, -40) * mm, "end": v(-74, -40) * mm});
            skLineSegment(sketch, "E108.MirrorCS", {"start": v(-45, -9.96) * mm, "end": v(-42, -9.96) * mm});
            skLineSegment(sketch, "E109.MirrorCS", {"start": v(-90, -40) * mm, "end": v(-5, -40) * mm});
            skLineSegment(sketch, "E110.MirrorCS", {"start": v(-21, -40) * mm, "end": v(-18, -40) * mm});
            skLineSegment(sketch, "E111.MirrorCS", {"start": v(-90, -9.96) * mm, "end": v(-5, -9.96) * mm});
            skLineSegment(sketch, "E112.MirrorCS", {"start": v(-85, -9.96) * mm, "end": v(-82, -9.96) * mm});
            skLineSegment(sketch, "E113.MirrorCS", {"start": v(-85, -40) * mm, "end": v(-82, -40) * mm});
            skLineSegment(sketch, "E114.MirrorCS", {"start": v(-37, -9.96) * mm, "end": v(-34, -9.96) * mm});
            skLineSegment(sketch, "E115.MirrorCS", {"start": v(-2, -40) * mm, "end": v(-2, -9.86) * mm});
            skLineSegment(sketch, "E116.MirrorCS", {"start": v(-10, -40) * mm, "end": v(-10, -9.96) * mm});
            skLineSegment(sketch, "E117.MirrorCS", {"start": v(-74, -40) * mm, "end": v(-74, -9.96) * mm});
            skLineSegment(sketch, "E118.MirrorCS", {"start": v(-66, -40) * mm, "end": v(-66, -9.96) * mm});
            skLineSegment(sketch, "E119.MirrorCS", {"start": v(-53, -40) * mm, "end": v(-53, -9.96) * mm});
            skLineSegment(sketch, "E120.MirrorCS", {"start": v(-13, -40) * mm, "end": v(-13, -9.96) * mm});
            skLineSegment(sketch, "E121.MirrorCS", {"start": v(-58, -40) * mm, "end": v(-58, -9.96) * mm});
            skLineSegment(sketch, "E122.MirrorCS", {"start": v(-50, -40) * mm, "end": v(-50, -9.96) * mm});
            skLineSegment(sketch, "E123.MirrorCS", {"start": v(-77, -40) * mm, "end": v(-77, -9.96) * mm});
            skLineSegment(sketch, "E124.MirrorCS", {"start": v(-69, -40) * mm, "end": v(-69, -9.96) * mm});
            skLineSegment(sketch, "E125.MirrorCS", {"start": v(-45, -40) * mm, "end": v(-45, -9.96) * mm});
            skLineSegment(sketch, "E126.MirrorCS", {"start": v(-34, -40) * mm, "end": v(-34, -9.96) * mm});
            skLineSegment(sketch, "E127.MirrorCS", {"start": v(-29, -40) * mm, "end": v(-29, -9.96) * mm});
            skLineSegment(sketch, "E128.MirrorCS", {"start": v(-26, -40) * mm, "end": v(-26, -9.96) * mm});
            skLineSegment(sketch, "E129.MirrorCS", {"start": v(-61, -40) * mm, "end": v(-61, -9.96) * mm});
            skLineSegment(sketch, "E130.MirrorCS", {"start": v(-18, -40) * mm, "end": v(-18, -9.96) * mm});
            skLineSegment(sketch, "E131.MirrorCS", {"start": v(-42, -40) * mm, "end": v(-42, -9.96) * mm});
            skLineSegment(sketch, "E132.MirrorCS", {"start": v(-21, -40) * mm, "end": v(-21, -9.96) * mm});
            skLineSegment(sketch, "E133.MirrorCS", {"start": v(-85, -40) * mm, "end": v(-85, -9.96) * mm});
            skLineSegment(sketch, "E134.MirrorCS", {"start": v(-37, -40) * mm, "end": v(-37, -9.96) * mm});
            skLineSegment(sketch, "E135.MirrorCS", {"start": v(-5, -40) * mm, "end": v(-5, -9.96) * mm});
            skLineSegment(sketch, "E136.MirrorCS", {"start": v(-82, -40) * mm, "end": v(-82, -9.96) * mm});
            skLineSegment(sketch, "E137", {"start": v(2, -9.86) * mm, "end": v(0, -9.96) * mm});
            skSolve(sketch);
        }
        {
            var Q0;
            {var subQ0=sQuery(id+"F7.wireOp",EDGE,"E126.MirrorCS");Q0=makeQuery(id+"F7.imprint","IMPRINT",FACE,{"disambiguationData":[TD([[makeQuery(id+"F7.imprint","IMPRINT",EDGE,{"derivedFrom":subQ0}),-1.0]])]});}
            var Q1;
            {var subQ0=sQuery(id+"F7.wireOp",EDGE,"E76.left");Q1=makeQuery(id+"F7.imprint","IMPRINT",FACE,{"disambiguationData":[TD([[makeQuery(id+"F7.imprint","IMPRINT",EDGE,{"derivedFrom":subQ0}),1.0]])]});}
            var Q2;
            {var subQ0=sQuery(id+"F7.wireOp",EDGE,"E77.right");Q2=makeQuery(id+"F7.imprint","IMPRINT",FACE,{"disambiguationData":[TD([[makeQuery(id+"F7.imprint","IMPRINT",EDGE,{"derivedFrom":subQ0}),1.0]])]});}
            var Q3;
            {var subQ0=sQuery(id+"F7.wireOp",EDGE,"E78.right");Q3=makeQuery(id+"F7.imprint","IMPRINT",FACE,{"disambiguationData":[TD([[makeQuery(id+"F7.imprint","IMPRINT",EDGE,{"derivedFrom":subQ0}),1.0]])]});}
            var Q4;
            Q4=makeQuery(id+"F7.imprint","IMPRINT",FACE,{"disambiguationData":[TD([[makeQuery(id+"F7.imprint","IMPRINT",EDGE,{"derivedFrom":sQuery(id+"F7.wireOp",EDGE,"E81.bottom")}),-1.0]])]});
            var Q5;
            Q5=makeQuery(id+"F7.imprint","IMPRINT",FACE,{"disambiguationData":[TD([[makeQuery(id+"F7.imprint","IMPRINT",EDGE,{"derivedFrom":sQuery(id+"F7.wireOp",EDGE,"E82.bottom")}),-1.0]])]});
            var Q6;
            {var subQ0=sQuery(id+"F7.wireOp",EDGE,"E79.right");Q6=makeQuery(id+"F7.imprint","IMPRINT",FACE,{"disambiguationData":[TD([[makeQuery(id+"F7.imprint","IMPRINT",EDGE,{"derivedFrom":subQ0}),1.0]])]});}
            var Q7;
            {var subQ0=sQuery(id+"F7.wireOp",EDGE,"E80.left");Q7=makeQuery(id+"F7.imprint","IMPRINT",FACE,{"disambiguationData":[TD([[makeQuery(id+"F7.imprint","IMPRINT",EDGE,{"derivedFrom":subQ0}),-1.0]])]});}
            var Q8;
            {var subQ0=sQuery(id+"F7.wireOp",EDGE,"E80.right");Q8=makeQuery(id+"F7.imprint","IMPRINT",FACE,{"disambiguationData":[TD([[makeQuery(id+"F7.imprint","IMPRINT",EDGE,{"derivedFrom":subQ0}),1.0]])]});}
            var Q9;
            {var subQ0=sQuery(id+"F7.wireOp",EDGE,"E84.right");Q9=makeQuery(id+"F7.imprint","IMPRINT",FACE,{"disambiguationData":[TD([[makeQuery(id+"F7.imprint","IMPRINT",EDGE,{"derivedFrom":subQ0}),1.0]])]});}
            var Q10;
            {var subQ0=sQuery(id+"F7.wireOp",EDGE,"E85.right");Q10=makeQuery(id+"F7.imprint","IMPRINT",FACE,{"disambiguationData":[TD([[makeQuery(id+"F7.imprint","IMPRINT",EDGE,{"derivedFrom":subQ0}),1.0]])]});}
            var Q11;
            {var subQ2=sQuery(id+"F7.wireOp",EDGE,"E86.right");Q11=makeQuery(id+"F7.imprint","IMPRINT",FACE,{"disambiguationData":[TD([[makeQuery(id+"F7.imprint","IMPRINT",EDGE,{"derivedFrom":subQ2}),1.0]])]});}
            var Q12;
            {var subQ0=sQuery(id+"F7.wireOp",EDGE,"E90");Q12=makeQuery(id+"F7.imprint","IMPRINT",FACE,{"disambiguationData":[TD([[makeQuery(id+"F7.imprint","IMPRINT",EDGE,{"derivedFrom":subQ0}),1.0]])]});}
            var Q13;
            {var subQ2=sQuery(id+"F7.wireOp",EDGE,"E116.MirrorCS");Q13=makeQuery(id+"F7.imprint","IMPRINT",FACE,{"disambiguationData":[TD([[makeQuery(id+"F7.imprint","IMPRINT",EDGE,{"derivedFrom":subQ2}),-1.0]])]});}
            var Q14;
            {var subQ2=sQuery(id+"F7.wireOp",EDGE,"E120.MirrorCS");Q14=makeQuery(id+"F7.imprint","IMPRINT",FACE,{"disambiguationData":[TD([[makeQuery(id+"F7.imprint","IMPRINT",EDGE,{"derivedFrom":subQ2}),1.0]])]});}
            var Q15;
            {var subQ2=sQuery(id+"F7.wireOp",EDGE,"E128.MirrorCS");Q15=makeQuery(id+"F7.imprint","IMPRINT",FACE,{"disambiguationData":[TD([[makeQuery(id+"F7.imprint","IMPRINT",EDGE,{"derivedFrom":subQ2}),-1.0]])]});}
            var Q16;
            {var subQ0=sQuery(id+"F7.wireOp",EDGE,"E131.MirrorCS");Q16=makeQuery(id+"F7.imprint","IMPRINT",FACE,{"disambiguationData":[TD([[makeQuery(id+"F7.imprint","IMPRINT",EDGE,{"derivedFrom":subQ0}),-1.0]])]});}
            var Q17;
            {var subQ0=sQuery(id+"F7.wireOp",EDGE,"E122.MirrorCS");Q17=makeQuery(id+"F7.imprint","IMPRINT",FACE,{"disambiguationData":[TD([[makeQuery(id+"F7.imprint","IMPRINT",EDGE,{"derivedFrom":subQ0}),-1.0]])]});}
            var Q18;
            {var subQ0=sQuery(id+"F7.wireOp",EDGE,"E119.MirrorCS");Q18=makeQuery(id+"F7.imprint","IMPRINT",FACE,{"disambiguationData":[TD([[makeQuery(id+"F7.imprint","IMPRINT",EDGE,{"derivedFrom":subQ0}),1.0]])]});}
            var Q19;
            {var subQ0=sQuery(id+"F7.wireOp",EDGE,"E118.MirrorCS");Q19=makeQuery(id+"F7.imprint","IMPRINT",FACE,{"disambiguationData":[TD([[makeQuery(id+"F7.imprint","IMPRINT",EDGE,{"derivedFrom":subQ0}),-1.0]])]});}
            var Q20;
            {var subQ0=sQuery(id+"F7.wireOp",EDGE,"E117.MirrorCS");Q20=makeQuery(id+"F7.imprint","IMPRINT",FACE,{"disambiguationData":[TD([[makeQuery(id+"F7.imprint","IMPRINT",EDGE,{"derivedFrom":subQ0}),-1.0]])]});}
            var Q21;
            {var subQ2=sQuery(id+"F7.wireOp",EDGE,"E123.MirrorCS");Q21=makeQuery(id+"F7.imprint","IMPRINT",FACE,{"disambiguationData":[TD([[makeQuery(id+"F7.imprint","IMPRINT",EDGE,{"derivedFrom":subQ2}),1.0]])]});}
            var Q22;
            {var subQ0=sQuery(id+"F7.wireOp",EDGE,"E76.right");Q22=makeQuery(id+"F7.imprint","IMPRINT",FACE,{"disambiguationData":[TD([[makeQuery(id+"F7.imprint","IMPRINT",EDGE,{"derivedFrom":subQ0}),-1.0]])]});}
            extrude(context, id + "F8", {"entities" : qUnion([Q0, Q1, Q2, Q3, Q4, Q5, Q6, Q7, Q8, Q9, Q10, Q11, Q12, Q13, Q14, Q15, Q16, Q17, Q18, Q19, Q20, Q21, Q22]), "operationType" : NewBodyOperationType.REMOVE, "oppositeDirection" : true, "depth" : 3 * mm, "offsetDistance" : 25 * mm});
        }
        {
            var Q0;
            Q0=makeQuery(id+"F2.opExtrude","CAP_FACE",FACE,{"disambiguationData":[OSD([sQuery(id+"F0.wireOp",EDGE,"E5.bottom"),sQuery(id+"F0.wireOp",EDGE,"E5.top"),sQuery(id+"F0.wireOp",EDGE,"E6.filletArc"),sQuery(id+"F0.wireOp",EDGE,"E7.filletArc"),sQuery(id+"F0.wireOp",EDGE,"E8.filletArc"),sQuery(id+"F0.wireOp",EDGE,"E9.filletArc"),sQuery(id+"F0.wireOp",EDGE,"E10.bottom"),sQuery(id+"F0.wireOp",EDGE,"E10.top"),sQuery(id+"F0.wireOp",EDGE,"E10.left"),sQuery(id+"F0.wireOp",EDGE,"E10.right"),sQuery(id+"F0.wireOp",EDGE,"E11.filletArc"),sQuery(id+"F0.wireOp",EDGE,"E12.filletArc"),sQuery(id+"F0.wireOp",EDGE,"E13.filletArc"),sQuery(id+"F0.wireOp",EDGE,"E14.filletArc")])],"isStart":false});
            var sketch = newSketch(context, id + "F9", { "sketchPlane" : qUnion([Q0])});
            skCircle(sketch, "E138", {"center": v(103.96, -21.74) * mm, "radius": 4 * mm});
            skCircle(sketch, "E139.MirrorC", {"center": v(-103.96, -21.74) * mm, "radius": 4 * mm});
            skCircle(sketch, "E140.MirrorC", {"center": v(103.96, 21.74) * mm, "radius": 4 * mm});
            skCircle(sketch, "E141.MirrorC", {"center": v(-103.96, 21.74) * mm, "radius": 4 * mm});
            skCircle(sketch, "E142", {"center": v(-54, -30) * mm, "radius": 4 * mm});
            skCircle(sketch, "E143.MirrorC", {"center": v(54, -30) * mm, "radius": 4 * mm});
            skCircle(sketch, "E144.MirrorC", {"center": v(-54, 30) * mm, "radius": 4 * mm});
            skCircle(sketch, "E145.MirrorC", {"center": v(54, 30) * mm, "radius": 4 * mm});
            skSolve(sketch);
        }
        {
            var Q0;
            Q0=makeQuery(id+"F9.imprint","IMPRINT",FACE,{"disambiguationData":[TD([[makeQuery(id+"F9.imprint","IMPRINT",EDGE,{"derivedFrom":sQuery(id+"F9.wireOp",EDGE,"E141.MirrorC")}),1.0]])]});
            var Q1;
            Q1=makeQuery(id+"F9.imprint","IMPRINT",FACE,{"disambiguationData":[TD([[makeQuery(id+"F9.imprint","IMPRINT",EDGE,{"derivedFrom":sQuery(id+"F9.wireOp",EDGE,"E139.MirrorC")}),-1.0]])]});
            var Q2;
            Q2=makeQuery(id+"F9.imprint","IMPRINT",FACE,{"disambiguationData":[TD([[makeQuery(id+"F9.imprint","IMPRINT",EDGE,{"derivedFrom":sQuery(id+"F9.wireOp",EDGE,"E144.MirrorC")}),-1.0]])]});
            var Q3;
            Q3=makeQuery(id+"F9.imprint","IMPRINT",FACE,{"disambiguationData":[TD([[makeQuery(id+"F9.imprint","IMPRINT",EDGE,{"derivedFrom":sQuery(id+"F9.wireOp",EDGE,"E142")}),1.0]])]});
            var Q4;
            Q4=makeQuery(id+"F9.imprint","IMPRINT",FACE,{"disambiguationData":[TD([[makeQuery(id+"F9.imprint","IMPRINT",EDGE,{"derivedFrom":sQuery(id+"F9.wireOp",EDGE,"E143.MirrorC")}),-1.0]])]});
            var Q5;
            Q5=makeQuery(id+"F9.imprint","IMPRINT",FACE,{"disambiguationData":[TD([[makeQuery(id+"F9.imprint","IMPRINT",EDGE,{"derivedFrom":sQuery(id+"F9.wireOp",EDGE,"E145.MirrorC")}),1.0]])]});
            var Q6;
            Q6=makeQuery(id+"F9.imprint","IMPRINT",FACE,{"disambiguationData":[TD([[makeQuery(id+"F9.imprint","IMPRINT",EDGE,{"derivedFrom":sQuery(id+"F9.wireOp",EDGE,"E140.MirrorC")}),-1.0]])]});
            var Q7;
            Q7=makeQuery(id+"F9.imprint","IMPRINT",FACE,{"disambiguationData":[TD([[makeQuery(id+"F9.imprint","IMPRINT",EDGE,{"derivedFrom":sQuery(id+"F9.wireOp",EDGE,"E138")}),1.0]])]});
            extrude(context, id + "F10", {"entities" : qUnion([Q0, Q1, Q2, Q3, Q4, Q5, Q6, Q7]), "operationType" : NewBodyOperationType.REMOVE, "oppositeDirection" : true, "depth" : 80 * mm, "offsetDistance" : 25 * mm});
        }
        {
            var Q0;
            Q0=makeQuery(id+"F2.opExtrude","CAP_FACE",FACE,{"disambiguationData":[OSD([sQuery(id+"F0.wireOp",EDGE,"E5.bottom"),sQuery(id+"F0.wireOp",EDGE,"E5.top"),sQuery(id+"F0.wireOp",EDGE,"E6.filletArc"),sQuery(id+"F0.wireOp",EDGE,"E7.filletArc"),sQuery(id+"F0.wireOp",EDGE,"E8.filletArc"),sQuery(id+"F0.wireOp",EDGE,"E9.filletArc"),sQuery(id+"F0.wireOp",EDGE,"E10.bottom"),sQuery(id+"F0.wireOp",EDGE,"E10.top"),sQuery(id+"F0.wireOp",EDGE,"E10.left"),sQuery(id+"F0.wireOp",EDGE,"E10.right"),sQuery(id+"F0.wireOp",EDGE,"E11.filletArc"),sQuery(id+"F0.wireOp",EDGE,"E12.filletArc"),sQuery(id+"F0.wireOp",EDGE,"E13.filletArc"),sQuery(id+"F0.wireOp",EDGE,"E14.filletArc")])],"isStart":true});
            var sketch = newSketch(context, id + "F11", { "sketchPlane" : qUnion([Q0])});
            skLineSegment(sketch, "E146.bottom", {"start": v(87.5, -35.23) * mm, "end": v(-87.5, -35.23) * mm});
            skLineSegment(sketch, "E146.top", {"start": v(87.5, 35.23) * mm, "end": v(-87.5, 35.23) * mm});
            skLineSegment(sketch, "E146.left", {"start": v(122.5, -0.23) * mm, "end": v(122.5, 0.23) * mm});
            skLineSegment(sketch, "E146.right", {"start": v(-122.5, -0.23) * mm, "end": v(-122.5, 0.23) * mm});
            skPoint(sketch, "E146.middle", {"position": v(0, 0) * mm});
            skPoint(sketch, "E147.visualSharp", {"position": v(-122.5, 35.23) * mm});
            skArc(sketch, "E147.filletArc", {"start": v(-87.5, 35.23) * mm, "mid": v(-112.25, 24.98) * mm, "end": v(-122.5, 0.23) * mm});
            skPoint(sketch, "E148.visualSharp", {"position": v(-122.5, -35.23) * mm});
            skArc(sketch, "E148.filletArc", {"start": v(-122.5, -0.23) * mm, "mid": v(-112.25, -24.98) * mm, "end": v(-87.5, -35.23) * mm});
            skPoint(sketch, "E149.visualSharp", {"position": v(122.5, -35.23) * mm});
            skArc(sketch, "E149.filletArc", {"start": v(87.5, -35.23) * mm, "mid": v(112.25, -24.98) * mm, "end": v(122.5, -0.23) * mm});
            skPoint(sketch, "E150.visualSharp", {"position": v(122.5, 35.23) * mm});
            skArc(sketch, "E150.filletArc", {"start": v(122.5, 0.23) * mm, "mid": v(112.25, 24.98) * mm, "end": v(87.5, 35.23) * mm});
            skSolve(sketch);
        }
        {
            var Q0;
            Q0=makeQuery(id+"F11.imprint","IMPRINT",FACE,{"disambiguationData":[TD([[makeQuery(id+"F11.imprint","IMPRINT",EDGE,{"derivedFrom":sQuery(id+"F11.wireOp",EDGE,"E146.bottom")}),-1.0]])]});
            var Q1;
            Q1=makeQuery(id+"F11.imprint","IMPRINT",FACE,{"disambiguationData":[TD([[makeQuery(id+"F11.imprint","IMPRINT",EDGE,{"derivedFrom":makeQuery(id+"F2.opExtrude","CAP_EDGE",EDGE,{"disambiguationData":[OSD([sQuery(id+"F0.wireOp",EDGE,"E10.bottom")])],"isStart":true})}),1.0]])]});
            extrude(context, id + "F12", {"entities" : qUnion([Q0, Q1]), "operationType" : NewBodyOperationType.REMOVE, "oppositeDirection" : true, "depth" : 25 * mm, "offsetDistance" : 25 * mm});
        }
        {
            var Q0;
            Q0=makeQuery(id+"F3.opExtrude","CAP_FACE",FACE,{"disambiguationData":[OSD([sQuery(id+"F0.wireOp",EDGE,"E10.bottom"),sQuery(id+"F0.wireOp",EDGE,"E10.top"),sQuery(id+"F0.wireOp",EDGE,"E10.left"),sQuery(id+"F0.wireOp",EDGE,"E10.right"),sQuery(id+"F0.wireOp",EDGE,"E11.filletArc"),sQuery(id+"F0.wireOp",EDGE,"E12.filletArc"),sQuery(id+"F0.wireOp",EDGE,"E13.filletArc"),sQuery(id+"F0.wireOp",EDGE,"E14.filletArc")])],"isStart":false});
            var sketch = newSketch(context, id + "F13", { "sketchPlane" : qUnion([Q0])});
            skPoint(sketch, "E151.middle", {"position": v(0, 0) * mm});
            skArc(sketch, "E152", {"start": v(-59.8, 17.5) * mm, "mid": v(-63.8, 21.5) * mm, "end": v(-67.8, 17.5) * mm});
            skArc(sketch, "E153", {"start": v(-43.8, 17.5) * mm, "mid": v(-47.8, 21.5) * mm, "end": v(-51.8, 17.5) * mm});
            skArc(sketch, "E154", {"start": v(-27.8, 17.5) * mm, "mid": v(-31.8, 21.5) * mm, "end": v(-35.8, 17.5) * mm});
            skArc(sketch, "E155", {"start": v(-11.8, 17.5) * mm, "mid": v(-15.8, 21.5) * mm, "end": v(-19.8, 17.5) * mm});
            skArc(sketch, "E156.MirrorC", {"start": v(43.8, 17.5) * mm, "mid": v(47.8, 21.5) * mm, "end": v(51.8, 17.5) * mm});
            skArc(sketch, "E157.MirrorC", {"start": v(59.8, 17.5) * mm, "mid": v(63.8, 21.5) * mm, "end": v(67.8, 17.5) * mm});
            skArc(sketch, "E158.MirrorC", {"start": v(-4.2, 17.5) * mm, "mid": v(-0.2, 21.5) * mm, "end": v(3.8, 17.5) * mm});
            skArc(sketch, "E159.MirrorC", {"start": v(11.8, 17.5) * mm, "mid": v(15.8, 21.5) * mm, "end": v(19.8, 17.5) * mm});
            skArc(sketch, "E160.MirrorC", {"start": v(27.8, 17.5) * mm, "mid": v(31.8, 21.5) * mm, "end": v(35.8, 17.5) * mm});
            skArc(sketch, "E161.MirrorC", {"start": v(-4.2, -17.5) * mm, "mid": v(-0.2, -21.5) * mm, "end": v(3.8, -17.5) * mm});
            skArc(sketch, "E162.MirrorC", {"start": v(27.8, -17.5) * mm, "mid": v(31.8, -21.5) * mm, "end": v(35.8, -17.5) * mm});
            skArc(sketch, "E163.MirrorC", {"start": v(59.8, -17.4) * mm, "mid": v(63.75, -21.5) * mm, "end": v(67.8, -17.5) * mm});
            skArc(sketch, "E164.MirrorC", {"start": v(43.8, -17.5) * mm, "mid": v(47.8, -21.5) * mm, "end": v(51.8, -17.5) * mm});
            skArc(sketch, "E165.MirrorC", {"start": v(-11.8, -17.5) * mm, "mid": v(-15.8, -21.5) * mm, "end": v(-19.8, -17.5) * mm});
            skArc(sketch, "E166.MirrorC", {"start": v(-27.8, -17.5) * mm, "mid": v(-31.8, -21.5) * mm, "end": v(-35.8, -17.5) * mm});
            skArc(sketch, "E167.MirrorC", {"start": v(-43.8, -17.5) * mm, "mid": v(-47.8, -21.5) * mm, "end": v(-51.8, -17.5) * mm});
            skArc(sketch, "E168.MirrorC", {"start": v(-59.8, -17.5) * mm, "mid": v(-63.8, -21.5) * mm, "end": v(-67.8, -17.5) * mm});
            skArc(sketch, "E169.MirrorC", {"start": v(11.8, -17.5) * mm, "mid": v(15.8, -21.5) * mm, "end": v(19.8, -17.5) * mm});
            skLineSegment(sketch, "E170", {"start": v(-67.8, 17.5) * mm, "end": v(-67.8, -17.5) * mm});
            skLineSegment(sketch, "E171", {"start": v(-59.8, 17.5) * mm, "end": v(-59.8, -17.5) * mm});
            skLineSegment(sketch, "E172", {"start": v(-51.8, 17.5) * mm, "end": v(-51.8, -17.5) * mm});
            skLineSegment(sketch, "E173", {"start": v(-43.8, 17.5) * mm, "end": v(-43.8, -17.5) * mm});
            skLineSegment(sketch, "E174", {"start": v(-35.8, 17.5) * mm, "end": v(-35.8, -17.5) * mm});
            skLineSegment(sketch, "E175", {"start": v(-27.8, 17.5) * mm, "end": v(-27.8, -17.5) * mm});
            skLineSegment(sketch, "E176", {"start": v(-19.8, 17.5) * mm, "end": v(-19.8, -17.5) * mm});
            skLineSegment(sketch, "E177", {"start": v(-11.8, 17.5) * mm, "end": v(-11.8, -17.5) * mm});
            skLineSegment(sketch, "E178", {"start": v(-4.2, 17.5) * mm, "end": v(-4.2, -17.5) * mm});
            skLineSegment(sketch, "E179", {"start": v(3.8, 17.5) * mm, "end": v(3.8, -17.5) * mm});
            skLineSegment(sketch, "E180", {"start": v(11.8, 17.5) * mm, "end": v(11.8, -17.5) * mm});
            skLineSegment(sketch, "E181", {"start": v(19.8, 17.5) * mm, "end": v(19.8, -17.5) * mm});
            skLineSegment(sketch, "E182", {"start": v(27.8, 17.5) * mm, "end": v(27.8, -17.5) * mm});
            skLineSegment(sketch, "E183", {"start": v(35.8, 17.5) * mm, "end": v(35.8, -17.5) * mm});
            skLineSegment(sketch, "E184", {"start": v(43.8, 17.5) * mm, "end": v(43.8, -17.5) * mm});
            skLineSegment(sketch, "E185", {"start": v(51.8, 17.5) * mm, "end": v(51.8, -17.5) * mm});
            skLineSegment(sketch, "E186", {"start": v(59.8, 17.5) * mm, "end": v(59.8, -17.4) * mm});
            skLineSegment(sketch, "E187", {"start": v(67.8, 17.5) * mm, "end": v(67.8, -17.5) * mm});
            skSolve(sketch);
        }
        {
            var Q0;
            Q0=makeQuery(id+"F13.imprint","IMPRINT",FACE,{"disambiguationData":[TD([[makeQuery(id+"F13.imprint","IMPRINT",EDGE,{"derivedFrom":sQuery(id+"F13.wireOp",EDGE,"E152")}),1.0]])]});
            var Q1;
            Q1=makeQuery(id+"F13.imprint","IMPRINT",FACE,{"disambiguationData":[TD([[makeQuery(id+"F13.imprint","IMPRINT",EDGE,{"derivedFrom":sQuery(id+"F13.wireOp",EDGE,"E153")}),1.0]])]});
            var Q2;
            Q2=makeQuery(id+"F13.imprint","IMPRINT",FACE,{"disambiguationData":[TD([[makeQuery(id+"F13.imprint","IMPRINT",EDGE,{"derivedFrom":sQuery(id+"F13.wireOp",EDGE,"E154")}),1.0]])]});
            var Q3;
            Q3=makeQuery(id+"F13.imprint","IMPRINT",FACE,{"disambiguationData":[TD([[makeQuery(id+"F13.imprint","IMPRINT",EDGE,{"derivedFrom":sQuery(id+"F13.wireOp",EDGE,"E155")}),1.0]])]});
            var Q4;
            Q4=makeQuery(id+"F13.imprint","IMPRINT",FACE,{"disambiguationData":[TD([[makeQuery(id+"F13.imprint","IMPRINT",EDGE,{"derivedFrom":sQuery(id+"F13.wireOp",EDGE,"E158.MirrorC")}),-1.0]])]});
            var Q5;
            Q5=makeQuery(id+"F13.imprint","IMPRINT",FACE,{"disambiguationData":[TD([[makeQuery(id+"F13.imprint","IMPRINT",EDGE,{"derivedFrom":sQuery(id+"F13.wireOp",EDGE,"E159.MirrorC")}),-1.0]])]});
            var Q6;
            Q6=makeQuery(id+"F13.imprint","IMPRINT",FACE,{"disambiguationData":[TD([[makeQuery(id+"F13.imprint","IMPRINT",EDGE,{"derivedFrom":sQuery(id+"F13.wireOp",EDGE,"E160.MirrorC")}),-1.0]])]});
            var Q7;
            Q7=makeQuery(id+"F13.imprint","IMPRINT",FACE,{"disambiguationData":[TD([[makeQuery(id+"F13.imprint","IMPRINT",EDGE,{"derivedFrom":sQuery(id+"F13.wireOp",EDGE,"E156.MirrorC")}),-1.0]])]});
            var Q8;
            {var subQ1=sQuery(id+"F13.wireOp",EDGE,"E157.MirrorC");Q8=makeQuery(id+"F13.imprint","IMPRINT",FACE,{"disambiguationData":[TD([[makeQuery(id+"F13.imprint","IMPRINT",EDGE,{"derivedFrom":subQ1}),-1.0]])]});}
            extrude(context, id + "F14", {"entities" : qUnion([Q0, Q1, Q2, Q3, Q4, Q5, Q6, Q7, Q8]), "operationType" : NewBodyOperationType.REMOVE, "oppositeDirection" : true, "depth" : 70 * mm, "offsetDistance" : 25 * mm});
        }
        {
            var Q0;
            {var subQ0=sQuery(id+"F0.wireOp",EDGE,"E10.left");var subQ1=sQuery(id+"F0.wireOp",EDGE,"E10.top");var subQ2=sQuery(id+"F0.wireOp",EDGE,"E10.right");var subQ3=sQuery(id+"F0.wireOp",EDGE,"E10.bottom");var subQ4=sQuery(id+"F0.wireOp",EDGE,"E11.filletArc");var subQ5=sQuery(id+"F0.wireOp",EDGE,"E12.filletArc");var subQ6=sQuery(id+"F0.wireOp",EDGE,"E13.filletArc");var subQ7=sQuery(id+"F0.wireOp",EDGE,"E14.filletArc");Q0=makeQuery(id+"F12.boolean.opBoolean","COPY",FACE,{"disambiguationData":[TD([makeQuery(id+"F3.opExtrude","SWEPT_FACE",FACE,{"disambiguationData":[OSD([subQ3])]})])],"derivedFrom":makeQuery(id+"F12.opExtrude","CAP_FACE",FACE,{"disambiguationData":[OSD([sQuery(id+"F0.wireOp",EDGE,"E5.bottom"),sQuery(id+"F0.wireOp",EDGE,"E5.top"),sQuery(id+"F0.wireOp",EDGE,"E6.filletArc"),sQuery(id+"F0.wireOp",EDGE,"E7.filletArc"),sQuery(id+"F0.wireOp",EDGE,"E8.filletArc"),sQuery(id+"F0.wireOp",EDGE,"E9.filletArc"),subQ3,subQ1,subQ0,subQ2,subQ4,subQ5,subQ6,subQ7,sQuery(id+"F9.wireOp",EDGE,"E138"),sQuery(id+"F9.wireOp",EDGE,"E139.MirrorC"),sQuery(id+"F9.wireOp",EDGE,"E140.MirrorC"),sQuery(id+"F9.wireOp",EDGE,"E141.MirrorC"),sQuery(id+"F9.wireOp",EDGE,"E142"),sQuery(id+"F9.wireOp",EDGE,"E143.MirrorC"),sQuery(id+"F9.wireOp",EDGE,"E144.MirrorC"),sQuery(id+"F9.wireOp",EDGE,"E145.MirrorC"),sQuery(id+"F11.wireOp",EDGE,"E146.bottom"),sQuery(id+"F11.wireOp",EDGE,"E146.top"),sQuery(id+"F11.wireOp",EDGE,"E146.left"),sQuery(id+"F11.wireOp",EDGE,"E146.right"),sQuery(id+"F11.wireOp",EDGE,"E147.filletArc"),sQuery(id+"F11.wireOp",EDGE,"E148.filletArc"),sQuery(id+"F11.wireOp",EDGE,"E149.filletArc"),sQuery(id+"F11.wireOp",EDGE,"E150.filletArc")])],"isStart":false})});}
            extrude(context, id + "F15", {"entities" : qUnion([Q0]), "operationType" : NewBodyOperationType.REMOVE, "oppositeDirection" : true, "depth" : 15 * mm, "offsetDistance" : 25 * mm});
        }
    });
